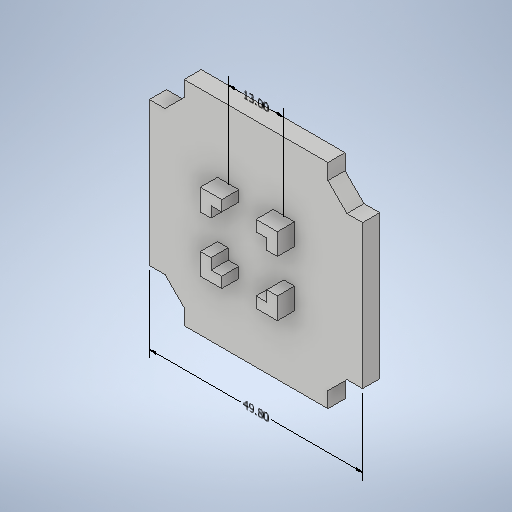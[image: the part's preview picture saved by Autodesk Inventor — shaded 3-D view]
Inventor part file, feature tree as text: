
AUTODESK INVENTOR PART (.ipt)
format: ipt  version: 2025 (Build 290162000, 162)  size: 300,032 bytes
history: native  units: mm
features: extrude x2, sketch x2, other x2
ambient origin geometry x8: Origin, YZ Plane, XZ Plane, XY Plane, X Axis, Y Axis, Z Axis, Center Point
bodies: 实体1 (feature_tree)
feature tree (6):
  extrude  "拉伸1"  Depth=4.0mm TaperAngle=0.0deg
  extrude  "拉伸2"  [1 undecoded]
  sketch  "草图1"  dims[d31=4.0mm d32=0.0mm d51=4.0mm d52=0.0mm]
  sketch  "草图2"  dims[d45=5.895245mm d46=4.635271mm d47=13.0mm d48=4.756255mm d49=5.78255mm d50=49.801261mm]
  other  "线性尺寸 1"
  other  "线性尺寸 2"
note: 1 required parameter value undecoded (feature->parameter linkage not recoverable at this tier; creation-order binding heuristic only, values carry confidence <= 0.55)
